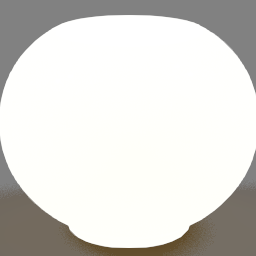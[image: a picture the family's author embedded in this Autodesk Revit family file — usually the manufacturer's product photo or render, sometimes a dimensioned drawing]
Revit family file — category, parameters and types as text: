
# Revit family: 3-1201-xx Perla Mirror
name_source: partatom
category: Luminarias
units: mm (PartAtom-declared; Revit-internal decimal feet)

## family parameters
Anfitrión = Muro
Compartido = No
Corte con vacíos al cargar = No
Cota de conector redondo = Diámetro de uso
Número OmniClass = 23.80.70.00
Origen de luz = No
Punto de cálculo de habitación = No
Siempre vertical = Sí
Tipo de pieza = Normal
Título OmniClass = Lighting

## types (3) — shared parameters
Fabricante = Vanita by Oxygen
Lámpara = LED Array
Metal Finish 1 = 15 - Black
Modelo = 3-020X-xx / Avior Round
References = Ref. 3 = 120 V / Ref. 37 = 277 V
URL = www.oxygenlighting.com
Voltage = 120 V
Voltage Input = 120 V or 277 V - 50/60 Hz
zero-valued in all types: Elevación por defecto

## per-type parameters (varying)
| type | Comentarios de vataje | Diameter |
| 3-0201-15 / Black | 1 x 26 W at 120 V | 762 mm  [stored 2.5 ft] |
| 3-0202-15 / Black | 1 x 50.7 W at 120 V | 914 mm  [stored 2.99869 ft] |
| 3-0203-15 / Black | 1 x 99.8 W at 120 V | 1219 mm |

note: [stored X ft] marks values corroborated as IEEE doubles in the binary element streams (Revit-internal decimal feet)

## geometry (parser evidence)
native form markers: Sweep x4
no freeform markers — native parametric forms only
